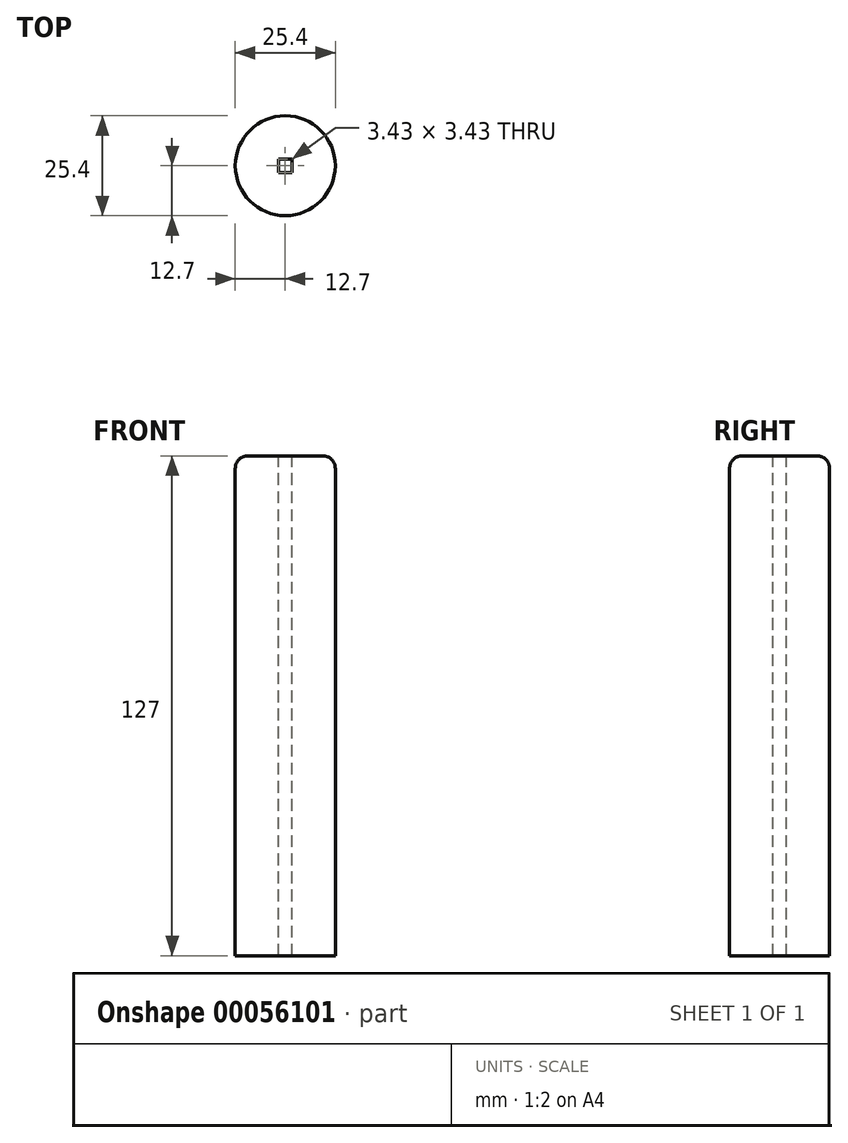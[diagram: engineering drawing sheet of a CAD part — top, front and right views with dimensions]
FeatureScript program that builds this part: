
annotation { "Feature Type Name" : "Feature", "Feature Type Description" : "" }
export const myFeature = defineFeature(function(context is Context, id is Id, definition is map)
    precondition{}
    {
        {
            var Q0;
            Q0=qCreatedBy(makeId("Top.planeOp"),FACE);
            var sketch = newSketch(context, id + "F0", { "sketchPlane" : qUnion([Q0])});
            skCircle(sketch, "E0", {"center": v(0, 0) * mm, "radius": 12.7 * mm});
            skSolve(sketch);
        }
        {
            var Q0;
            Q0=makeQuery(id+"F0.imprint","IMPRINT",FACE,{"disambiguationData":[TD([[makeQuery(id+"F0.imprint","IMPRINT",EDGE,{"derivedFrom":sQuery(id+"F0.wireOp",EDGE,"E0")}),1.0]])]});
            extrude(context, id + "F1", {"entities" : qUnion([Q0]), "depth" : 127 * mm});
        }
        {
            var Q0;
            Q0=makeQuery(id+"F1.opExtrude","CAP_EDGE",EDGE,{"disambiguationData":[OSD([sQuery(id+"F0.wireOp",EDGE,"E0")])],"isStart":false});
            fillet(context, id + "F2", {"entities" : qUnion([Q0]), "radius" : 3.17 * mm, "tangentPropagation" : true, "allowEdgeOverflow" : false});
        }
        {
            var Q0;
            Q0=makeQuery(id+"F1.opExtrude","CAP_FACE",FACE,{"disambiguationData":[OSD([sQuery(id+"F0.wireOp",EDGE,"E0")])],"isStart":false});
            var sketch = newSketch(context, id + "F3", { "sketchPlane" : qUnion([Q0])});
            skLineSegment(sketch, "E1.rect.bottom", {"start": v(1.71, 1.71) * mm, "end": v(-1.71, 1.71) * mm});
            skLineSegment(sketch, "E1.rect.top", {"start": v(1.71, -1.71) * mm, "end": v(-1.71, -1.71) * mm});
            skLineSegment(sketch, "E1.rect.left", {"start": v(1.71, 1.71) * mm, "end": v(1.71, -1.71) * mm});
            skLineSegment(sketch, "E1.rect.right", {"start": v(-1.71, 1.71) * mm, "end": v(-1.71, -1.71) * mm});
            skPoint(sketch, "E1.rect.middle", {"position": v(0, 0) * mm});
            skSolve(sketch);
        }
        {
            var Q0;
            Q0=makeQuery(id+"F3.imprint","IMPRINT",FACE,{"disambiguationData":[TD([[makeQuery(id+"F3.imprint","IMPRINT",EDGE,{"derivedFrom":sQuery(id+"F3.wireOp",EDGE,"E1.rect.bottom")}),1.0]])]});
            extrude(context, id + "F4", {"entities" : qUnion([Q0]), "operationType" : NewBodyOperationType.REMOVE, "endBound" : BoundingType.THROUGH_ALL, "oppositeDirection" : true, "depth" : 25.4 * mm});
        }
    });
